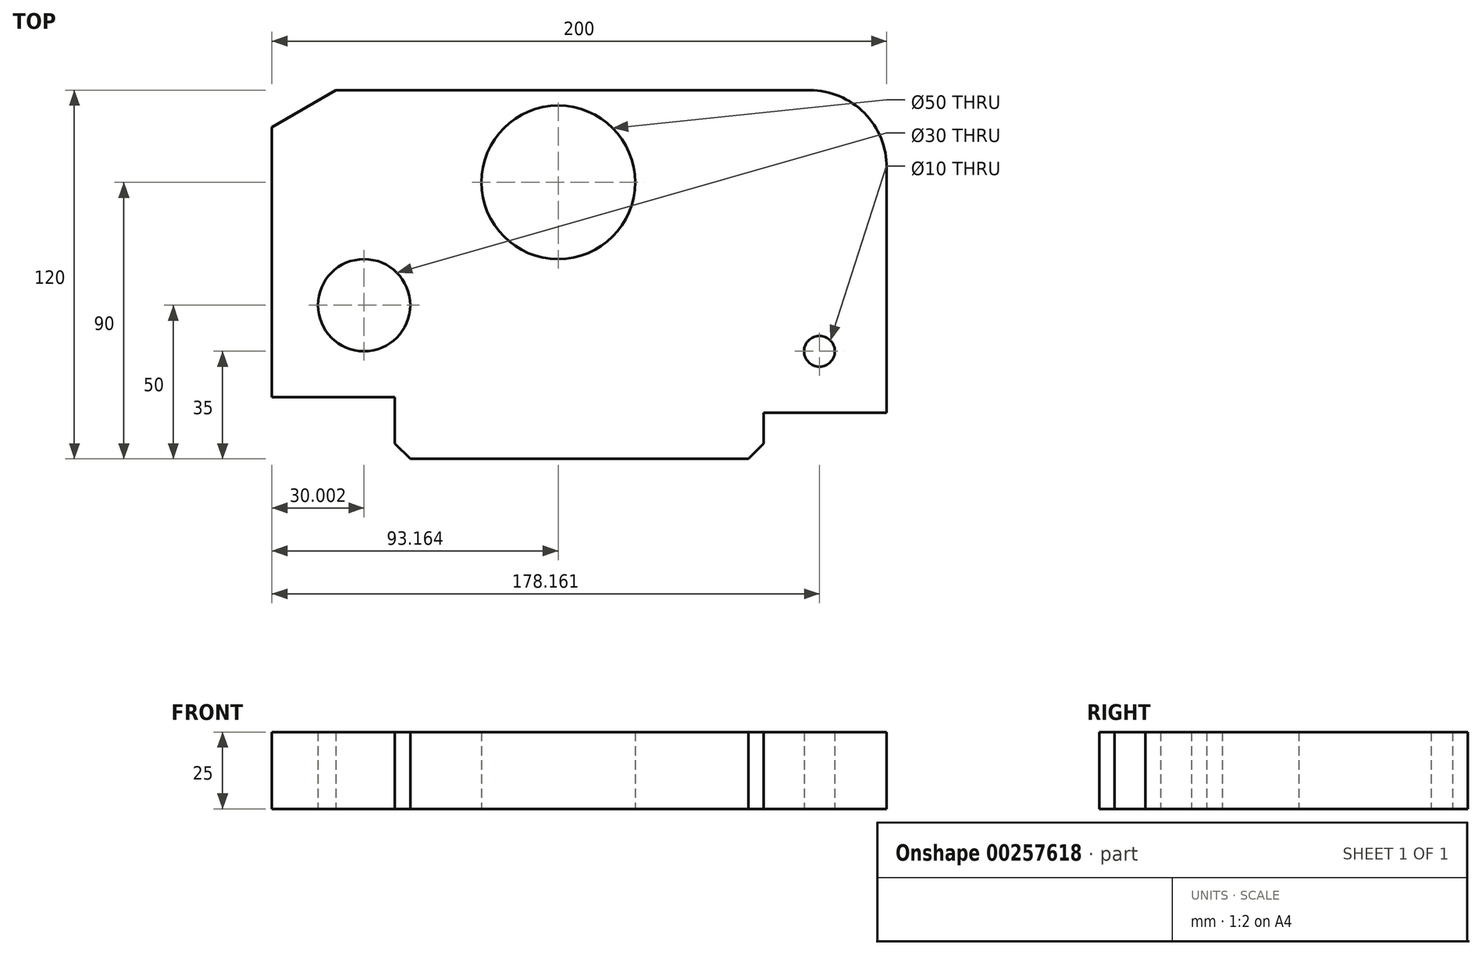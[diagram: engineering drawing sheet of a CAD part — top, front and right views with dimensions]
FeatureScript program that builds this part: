
annotation { "Feature Type Name" : "Feature", "Feature Type Description" : "" }
export const myFeature = defineFeature(function(context is Context, id is Id, definition is map)
    precondition{}
    {
        {
            var Q0;
            Q0=qCreatedBy(makeId("Top.planeOp"),FACE);
            var sketch = newSketch(context, id + "F0", { "sketchPlane" : qUnion([Q0])});
            skLineSegment(sketch, "E0", {"start": v(-63.1, 22.32) * mm, "end": v(-63.1, -35.68) * mm});
            skLineSegment(sketch, "E1", {"start": v(-63.1, 22.32) * mm, "end": v(-42.31, 34.32) * mm});
            skLineSegment(sketch, "E2", {"start": v(-42.31, 34.32) * mm, "end": v(111.9, 34.32) * mm});
            skPoint(sketch, "E3.visualSharp", {"position": v(139.03, 34.32) * mm});
            skArc(sketch, "E3.filletArc", {"start": v(136.9, 9.08) * mm, "mid": v(129.67, 26.91) * mm, "end": v(111.9, 34.32) * mm});
            skLineSegment(sketch, "E4", {"start": v(-42.31, 34.32) * mm, "end": v(28.69, 34.32) * mm});
            skLineSegment(sketch, "E5", {"start": v(28.69, 34.32) * mm, "end": v(-1.31, 34.32) * mm});
            skCircle(sketch, "E6", {"center": v(30.06, 4.32) * mm, "radius": 25 * mm});
            skLineSegment(sketch, "E7", {"start": v(-63.1, -35.68) * mm, "end": v(-63.1, -65.68) * mm});
            skLineSegment(sketch, "E8", {"start": v(-63.1, -65.68) * mm, "end": v(-23.1, -65.68) * mm});
            skLineSegment(sketch, "E9", {"start": v(-23.1, -65.68) * mm, "end": v(-23.1, -80.68) * mm});
            skLineSegment(sketch, "E10", {"start": v(-23.1, -80.68) * mm, "end": v(-18.1, -85.68) * mm});
            skLineSegment(sketch, "E11", {"start": v(96.9, -80.68) * mm, "end": v(96.9, -70.68) * mm});
            skLineSegment(sketch, "E12", {"start": v(96.9, -70.68) * mm, "end": v(136.9, -70.68) * mm});
            skLineSegment(sketch, "E13", {"start": v(96.9, -80.68) * mm, "end": v(91.9, -85.68) * mm});
            skLineSegment(sketch, "E14", {"start": v(-18.1, -85.68) * mm, "end": v(91.9, -85.68) * mm});
            skLineSegment(sketch, "E15", {"start": v(-63.1, -65.68) * mm, "end": v(-33.1, -65.68) * mm});
            skCircle(sketch, "E16", {"center": v(-33.1, -35.68) * mm, "radius": 15 * mm});
            skLineSegment(sketch, "E17", {"start": v(136.9, -70.68) * mm, "end": v(116.9, -70.68) * mm});
            skCircle(sketch, "E18", {"center": v(115.06, -50.68) * mm, "radius": 5 * mm});
            skLineSegment(sketch, "E19", {"start": v(136.9, 9.08) * mm, "end": v(136.9, -70.68) * mm});
            skSolve(sketch);
        }
        {
            var Q0;
            Q0=makeQuery(id+"F0.imprint","IMPRINT",FACE,{"disambiguationData":[TD([[makeQuery(id+"F0.imprint","IMPRINT",EDGE,{"derivedFrom":sQuery(id+"F0.wireOp",EDGE,"E0")}),1.0]])]});
            extrude(context, id + "F1", {"entities" : qUnion([Q0]), "depth" : 25 * mm});
        }
    });
